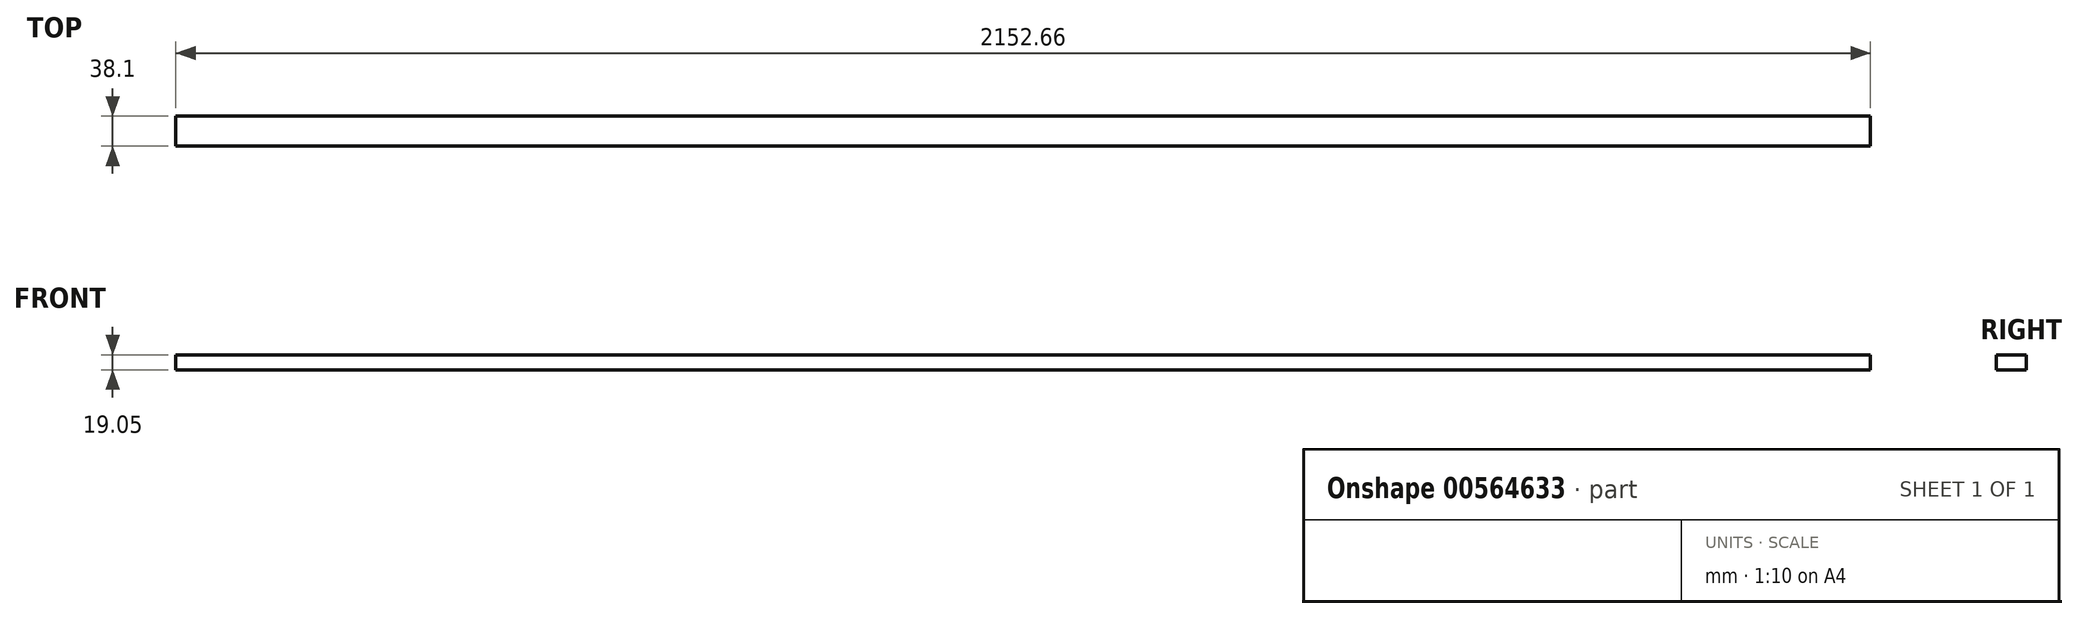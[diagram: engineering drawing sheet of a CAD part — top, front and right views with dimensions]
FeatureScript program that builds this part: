
annotation { "Feature Type Name" : "Feature", "Feature Type Description" : "" }
export const myFeature = defineFeature(function(context is Context, id is Id, definition is map)
    precondition{}
    {
        {
            var Q0;
            Q0=qCreatedBy(makeId("Top.planeOp"),FACE);
            var sketch = newSketch(context, id + "F0", { "sketchPlane" : qUnion([Q0])});
            skLineSegment(sketch, "E0.bottom", {"start": v(-1076.33, 19.05) * mm, "end": v(1076.33, 19.05) * mm});
            skLineSegment(sketch, "E0.top", {"start": v(-1076.33, -19.05) * mm, "end": v(1076.33, -19.05) * mm});
            skLineSegment(sketch, "E0.left", {"start": v(-1076.33, 19.05) * mm, "end": v(-1076.33, -19.05) * mm});
            skLineSegment(sketch, "E0.right", {"start": v(1076.33, 19.05) * mm, "end": v(1076.33, -19.05) * mm});
            skPoint(sketch, "E0.middle", {"position": v(0, 0) * mm});
            skSolve(sketch);
        }
        {
            var Q0;
            Q0=makeQuery(id+"F0.imprint","IMPRINT",FACE,{"disambiguationData":[TD([[makeQuery(id+"F0.imprint","IMPRINT",EDGE,{"derivedFrom":sQuery(id+"F0.wireOp",EDGE,"E0.bottom")}),-1.0]])]});
            extrude(context, id + "F1", {"entities" : qUnion([Q0]), "depth" : 19.05 * mm, "offsetDistance" : 25.4 * mm});
        }
    });
